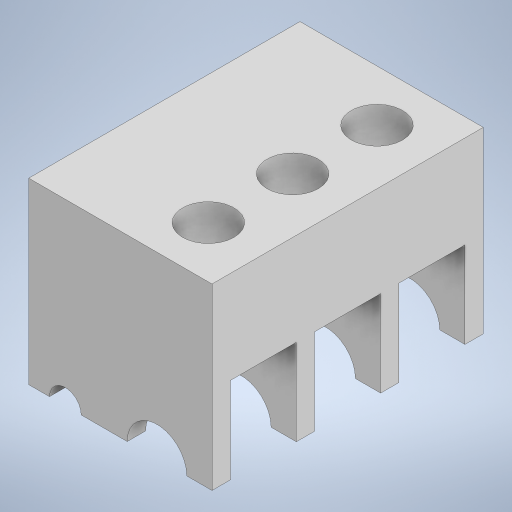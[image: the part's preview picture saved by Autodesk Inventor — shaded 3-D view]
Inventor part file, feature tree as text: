
AUTODESK INVENTOR PART (.ipt)
format: ipt  version: 2023 (Build 270158000, 158)  size: 342,016 bytes
history: native  units: in
note: dims shown in document units (in); Inventor stores cm internally (conversion verified against a paired STEP export)
features: extrude x4, sketch x3
ambient origin geometry x8: Origin, YZ Plane, XZ Plane, XY Plane, X Axis, Y Axis, Z Axis, Center Point
bodies: Solid1 (feature_tree)
feature tree (7):
  extrude  "Extrusion1"  Depth=4.878in
  sketch  "Sketch2"  dims[d2=1.625in d3=7.4in d4=0.0in]
  extrude  "Extrusion2"  Depth=7.4in TaperAngle=0.0deg
  extrude  "Extrusion3"  Depth=1.5in
  extrude  "Extrusion4"  Depth=1.5in
  sketch  "Sketch1"  dims[d0=5.0in d1=4.878in]
  sketch  "Sketch4"  dims[d6=1.4in d7=1.5in d10=1.4in d11=1.5in d13=2.3in d14=1.5in d15=1.4in d16=3.7in d17=6.0in d18=0.5in d20=2.528in d21=7.4in d22=0.0in d23=7.4in d24=0.0in d25=1.5in d26=0.866in d27=1.5in d28=0.0in d29=1.4in d30=0.0in d31=0.0in d32=0.0in]
